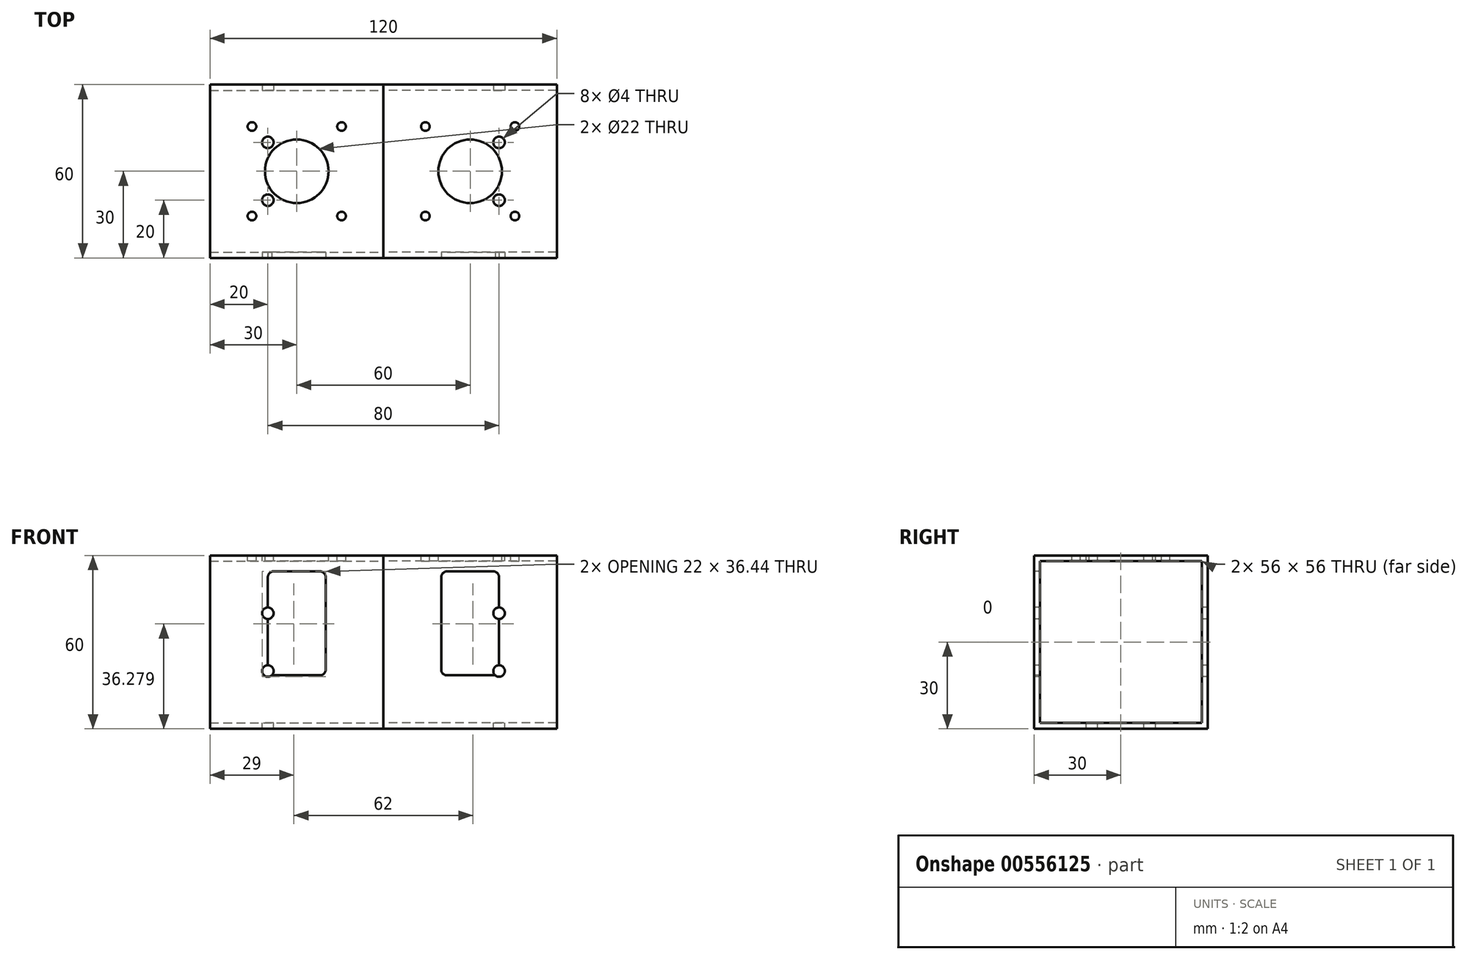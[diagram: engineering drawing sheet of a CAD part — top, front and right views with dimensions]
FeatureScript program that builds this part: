
annotation { "Feature Type Name" : "Feature", "Feature Type Description" : "" }
export const myFeature = defineFeature(function(context is Context, id is Id, definition is map)
    precondition{}
    {
        {
            var Q0;
            Q0=qCreatedBy(makeId("Right.planeOp"),FACE);
            var sketch = newSketch(context, id + "F0", { "sketchPlane" : qUnion([Q0])});
            skLineSegment(sketch, "E0.bottom", {"start": v(30, 30) * mm, "end": v(-30, 30) * mm});
            skLineSegment(sketch, "E0.top", {"start": v(30, -30) * mm, "end": v(-30, -30) * mm});
            skLineSegment(sketch, "E0.left", {"start": v(30, 30) * mm, "end": v(30, -30) * mm});
            skLineSegment(sketch, "E0.right", {"start": v(-30, 30) * mm, "end": v(-30, -30) * mm});
            skPoint(sketch, "E0.middle", {"position": v(0, 0) * mm});
            skSolve(sketch);
        }
        {
            var Q0;
            Q0=qSketchRegion(id+"F0",true);
            extrude(context, id + "F1", {"entities" : qUnion([Q0]), "oppositeDirection" : true, "depth" : 60 * mm, "offsetDistance" : 25 * mm});
        }
        {
            var Q0;
            Q0=makeQuery(id+"F1.opExtrude","CAP_FACE",FACE,{"disambiguationData":[OSD([sQuery(id+"F0.wireOp",EDGE,"E0.bottom"),sQuery(id+"F0.wireOp",EDGE,"E0.top"),sQuery(id+"F0.wireOp",EDGE,"E0.left"),sQuery(id+"F0.wireOp",EDGE,"E0.right")])],"isStart":false});
            var Q1;
            Q1=makeQuery(id+"F1.opExtrude","CAP_FACE",FACE,{"disambiguationData":[OSD([sQuery(id+"F0.wireOp",EDGE,"E0.bottom"),sQuery(id+"F0.wireOp",EDGE,"E0.top"),sQuery(id+"F0.wireOp",EDGE,"E0.left"),sQuery(id+"F0.wireOp",EDGE,"E0.right")])],"isStart":true});
            shell(context, id + "F2", {"entities" : qUnion([Q0, Q1]), "thickness" : 2 * mm});
        }
        {
            var Q0;
            Q0=makeQuery(id+"F1.opExtrude","SWEPT_FACE",FACE,{"disambiguationData":[OSD([sQuery(id+"F0.wireOp",EDGE,"E0.bottom")])]});
            var sketch = newSketch(context, id + "F3", { "sketchPlane" : qUnion([Q0])});
            skPoint(sketch, "E1", {"position": v(-30, 0) * mm});
            skLineSegment(sketch, "E2", {"start": v(-60, 0) * mm, "end": v(0, 0) * mm, "construction": true});
            skLineSegment(sketch, "E3.bottom", {"start": v(-14.5, 15.5) * mm, "end": v(-45.5, 15.5) * mm, "construction": true});
            skLineSegment(sketch, "E3.top", {"start": v(-14.5, -15.5) * mm, "end": v(-45.5, -15.5) * mm, "construction": true});
            skLineSegment(sketch, "E3.left", {"start": v(-14.5, 15.5) * mm, "end": v(-14.5, -15.5) * mm, "construction": true});
            skLineSegment(sketch, "E3.right", {"start": v(-45.5, 15.5) * mm, "end": v(-45.5, -15.5) * mm, "construction": true});
            skLineSegment(sketch, "E4", {"start": v(-40, 30) * mm, "end": v(-40, -30) * mm, "construction": true});
            skPoint(sketch, "E5", {"position": v(-40, -10) * mm});
            skPoint(sketch, "E6", {"position": v(-40, 10) * mm});
            skSolve(sketch);
        }
        {
            var Q0;
            Q0=sQuery(id+"F3.wireOp",VERTEX,"E6");
            var Q1;
            Q1=sQuery(id+"F3.wireOp",VERTEX,"E5");
            var Q2;
            Q2=makeQuery(id+"F1.opExtrude","SWEPT_BODY",BODY,{"disambiguationData":[OSD([sQuery(id+"F0.wireOp",EDGE,"E0.bottom"),sQuery(id+"F0.wireOp",EDGE,"E0.top"),sQuery(id+"F0.wireOp",EDGE,"E0.left"),sQuery(id+"F0.wireOp",EDGE,"E0.right")])]});
            hole(context, id + "F4", {"style" : HoleStyle.SIMPLE, "endStyle" : HoleEndStyle.THROUGH, "holeDiameter" : 4 * mm, "majorDiameter" : 5 * mm, "isTappedThrough" : true, "tappedDepth" : 12 * mm, "tapClearance" : 3, "startFromSketch" : true, "locations" : qUnion([Q0, Q1]), "scope" : qUnion([Q2])});
        }
        {
            var Q0;
            Q0=sQuery(id+"F3.wireOp",VERTEX,"E1");
            var Q1;
            Q1=makeQuery(id+"F1.opExtrude","SWEPT_BODY",BODY,{"disambiguationData":[OSD([sQuery(id+"F0.wireOp",EDGE,"E0.bottom"),sQuery(id+"F0.wireOp",EDGE,"E0.top"),sQuery(id+"F0.wireOp",EDGE,"E0.left"),sQuery(id+"F0.wireOp",EDGE,"E0.right")])]});
            hole(context, id + "F5", {"style" : HoleStyle.SIMPLE, "endStyle" : HoleEndStyle.BLIND, "holeDiameter" : 22 * mm, "majorDiameter" : 5 * mm, "holeDepth" : 2 * mm, "isTappedThrough" : true, "tappedDepth" : 12 * mm, "tapClearance" : 3, "startFromSketch" : true, "locations" : qUnion([Q0]), "scope" : qUnion([Q1])});
        }
        {
            var Q0;
            Q0=sQuery(id+"F3.wireOp",VERTEX,"E3.right.start");
            var Q1;
            Q1=sQuery(id+"F3.wireOp",VERTEX,"E3.bottom.start");
            var Q2;
            Q2=sQuery(id+"F3.wireOp",VERTEX,"E3.top.start");
            var Q3;
            Q3=sQuery(id+"F3.wireOp",VERTEX,"E3.right.end");
            var Q4;
            Q4=makeQuery(id+"F1.opExtrude","SWEPT_BODY",BODY,{"disambiguationData":[OSD([sQuery(id+"F0.wireOp",EDGE,"E0.bottom"),sQuery(id+"F0.wireOp",EDGE,"E0.top"),sQuery(id+"F0.wireOp",EDGE,"E0.left"),sQuery(id+"F0.wireOp",EDGE,"E0.right")])]});
            hole(context, id + "F6", {"style" : HoleStyle.SIMPLE, "endStyle" : HoleEndStyle.BLIND, "holeDiameter" : 3 * mm, "majorDiameter" : 5 * mm, "holeDepth" : 2 * mm, "isTappedThrough" : true, "tappedDepth" : 12 * mm, "tapClearance" : 3, "startFromSketch" : true, "locations" : qUnion([Q0, Q1, Q2, Q3]), "scope" : qUnion([Q4])});
        }
        {
            var Q0;
            Q0=makeQuery(id+"F1.opExtrude","SWEPT_FACE",FACE,{"disambiguationData":[OSD([sQuery(id+"F0.wireOp",EDGE,"E0.right")])]});
            var sketch = newSketch(context, id + "F7", { "sketchPlane" : qUnion([Q0])});
            skLineSegment(sketch, "E7", {"start": v(-60, 0) * mm, "end": v(0, 0) * mm, "construction": true});
            skLineSegment(sketch, "E8.bottom", {"start": v(-20, 24.5) * mm, "end": v(-40, 24.5) * mm});
            skLineSegment(sketch, "E8.top", {"start": v(-20, -11.5) * mm, "end": v(-40, -11.5) * mm});
            skLineSegment(sketch, "E8.left", {"start": v(-20, 24.5) * mm, "end": v(-20, -11.5) * mm});
            skLineSegment(sketch, "E8.right", {"start": v(-40, 24.5) * mm, "end": v(-40, -11.5) * mm});
            skPoint(sketch, "E8.middle", {"position": v(-30, 6.5) * mm});
            skLineSegment(sketch, "E9", {"start": v(-40, 30) * mm, "end": v(-40, -30) * mm, "construction": true});
            skPoint(sketch, "E10", {"position": v(-40, 10) * mm});
            skPoint(sketch, "E11", {"position": v(-40, -10) * mm});
            skLineSegment(sketch, "E12", {"start": v(-30, 30) * mm, "end": v(-30, -30) * mm, "construction": true});
            skSolve(sketch);
        }
        {
            var Q0;
            Q0=sQuery(id+"F7.wireOp",VERTEX,"E10");
            var Q1;
            Q1=sQuery(id+"F7.wireOp",VERTEX,"E11");
            var Q2;
            Q2=makeQuery(id+"F1.opExtrude","SWEPT_BODY",BODY,{"disambiguationData":[OSD([sQuery(id+"F0.wireOp",EDGE,"E0.bottom"),sQuery(id+"F0.wireOp",EDGE,"E0.top"),sQuery(id+"F0.wireOp",EDGE,"E0.left"),sQuery(id+"F0.wireOp",EDGE,"E0.right")])]});
            hole(context, id + "F8", {"style" : HoleStyle.SIMPLE, "endStyle" : HoleEndStyle.THROUGH, "holeDiameter" : 4 * mm, "majorDiameter" : 5 * mm, "isTappedThrough" : true, "tappedDepth" : 12 * mm, "tapClearance" : 3, "startFromSketch" : true, "locations" : qUnion([Q0, Q1]), "scope" : qUnion([Q2])});
        }
        {
            var Q0;
            Q0 = qSketchRegion(id + "F7", true);
            extrude(context, id + "F9", {"entities" : qUnion([Q0]), "operationType" : NewBodyOperationType.REMOVE, "oppositeDirection" : true, "depth" : 2 * mm, "offsetDistance" : 25 * mm});
        }
        {
            var Q0;
            Q0=makeQuery(id+"F9.boolean.opBoolean","COPY",EDGE,{"derivedFrom":makeQuery(id+"F9.opExtrude","SWEPT_EDGE",EDGE,{"disambiguationData":[OSD([sQuery(id+"F7.wireOp",EDGE,"E8.bottom"),sQuery(id+"F7.wireOp",EDGE,"E8.right")])]})});
            var Q1;
            Q1=makeQuery(id+"F9.boolean.opBoolean","COPY",EDGE,{"derivedFrom":makeQuery(id+"F9.opExtrude","SWEPT_EDGE",EDGE,{"disambiguationData":[OSD([sQuery(id+"F7.wireOp",EDGE,"E8.bottom"),sQuery(id+"F7.wireOp",EDGE,"E8.left")])]})});
            var Q2;
            Q2=makeQuery(id+"F9.boolean.opBoolean","COPY",EDGE,{"derivedFrom":makeQuery(id+"F9.opExtrude","SWEPT_EDGE",EDGE,{"disambiguationData":[OSD([sQuery(id+"F7.wireOp",EDGE,"E8.top"),sQuery(id+"F7.wireOp",EDGE,"E8.left")])]})});
            var Q3;
            Q3=makeQuery(id+"F9.boolean.opBoolean","COPY",EDGE,{"derivedFrom":makeQuery(id+"F9.opExtrude","SWEPT_EDGE",EDGE,{"disambiguationData":[OSD([sQuery(id+"F7.wireOp",EDGE,"E8.top"),sQuery(id+"F7.wireOp",EDGE,"E8.right")])]})});
            fillet(context, id + "F10", {"entities" : qUnion([Q0, Q1, Q2, Q3]), "radius" : 2 * mm, "tangentPropagation" : true, "allowEdgeOverflow" : false});
        }
        {
            var Q0;
            Q0=makeQuery(id+"F1.opExtrude","SWEPT_BODY",BODY,{"disambiguationData":[OSD([sQuery(id+"F0.wireOp",EDGE,"E0.bottom"),sQuery(id+"F0.wireOp",EDGE,"E0.top"),sQuery(id+"F0.wireOp",EDGE,"E0.left"),sQuery(id+"F0.wireOp",EDGE,"E0.right")])]});
            var Q1;
            Q1=qCreatedBy(makeId("Right.planeOp"),FACE);
            mirror(context, id + "F11", {"entities" : qUnion([Q0]), "mirrorPlane" : qUnion([Q1])});
        }
    });
